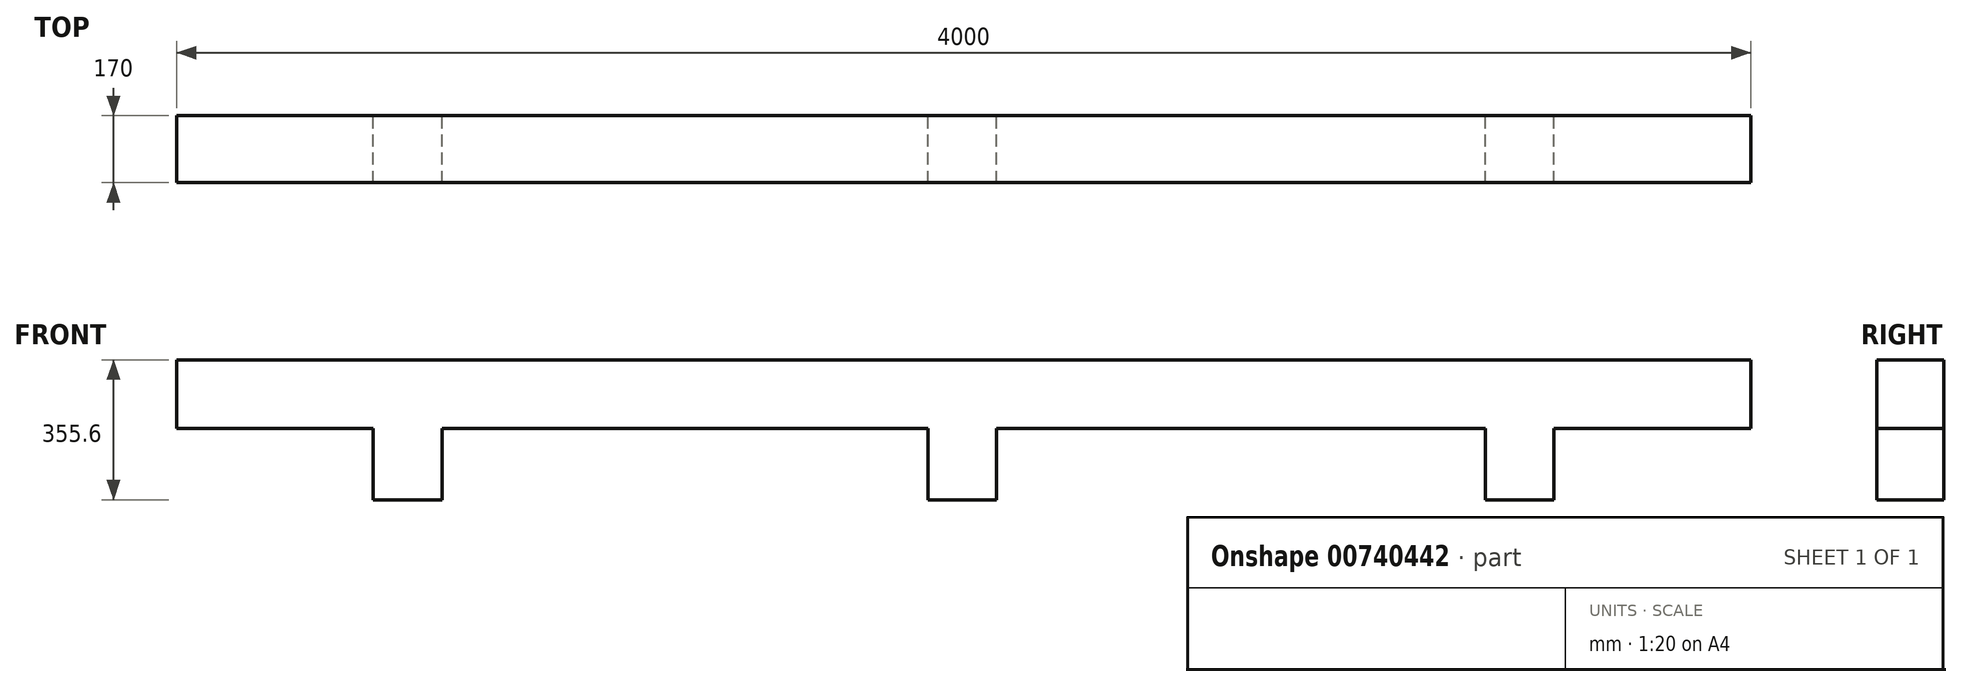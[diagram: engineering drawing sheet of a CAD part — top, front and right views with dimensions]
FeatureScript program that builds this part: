
annotation { "Feature Type Name" : "Feature", "Feature Type Description" : "" }
export const myFeature = defineFeature(function(context is Context, id is Id, definition is map)
    precondition{}
    {
        {
            var Q0;
            Q0=qCreatedBy(makeId("Front.planeOp"),FACE);
            var sketch = newSketch(context, id + "F0", { "sketchPlane" : qUnion([Q0])});
            skLineSegment(sketch, "E0", {"start": v(2000, 0) * mm, "end": v(-2000, 0) * mm, "construction": true});
            skLineSegment(sketch, "E1.bottom", {"start": v(-1997.52, 180.6) * mm, "end": v(-1497.52, 180.6) * mm});
            skLineSegment(sketch, "E1.top", {"start": v(-1997.52, 355.6) * mm, "end": v(2002.48, 355.6) * mm});
            skLineSegment(sketch, "E1.left", {"start": v(-1997.52, 180.6) * mm, "end": v(-1997.52, 355.6) * mm});
            skLineSegment(sketch, "E1.right", {"start": v(2002.48, 180.6) * mm, "end": v(2002.48, 355.6) * mm});
            skLineSegment(sketch, "E2.top", {"start": v(-1497.52, 0) * mm, "end": v(-1322.52, 0) * mm});
            skLineSegment(sketch, "E2.left", {"start": v(-1497.52, 180.6) * mm, "end": v(-1497.52, 0) * mm});
            skLineSegment(sketch, "E2.right", {"start": v(-1322.52, 180.6) * mm, "end": v(-1322.52, 0) * mm});
            skLineSegment(sketch, "E3.top", {"start": v(1502.48, 0) * mm, "end": v(1327.48, 0) * mm});
            skLineSegment(sketch, "E3.left", {"start": v(1502.48, 180.6) * mm, "end": v(1502.48, 0) * mm});
            skLineSegment(sketch, "E3.right", {"start": v(1327.48, 180.6) * mm, "end": v(1327.48, 0) * mm});
            skLineSegment(sketch, "E4.bottom", {"start": v(86.36, 0) * mm, "end": v(-88.64, 0) * mm});
            skLineSegment(sketch, "E4.left", {"start": v(86.36, 0) * mm, "end": v(86.36, 180.6) * mm});
            skLineSegment(sketch, "E4.right", {"start": v(-88.64, 0) * mm, "end": v(-88.64, 180.6) * mm});
            skLineSegment(sketch, "E5.trimOffspring", {"start": v(86.36, 180.6) * mm, "end": v(1327.48, 180.6) * mm});
            skLineSegment(sketch, "E6.trimOffspring", {"start": v(-1322.52, 180.6) * mm, "end": v(-88.64, 180.6) * mm});
            skLineSegment(sketch, "E7.trimOffspring", {"start": v(1502.48, 180.6) * mm, "end": v(2002.48, 180.6) * mm});
            skSolve(sketch);
        }
        {
            var Q0;
            Q0=makeQuery(id+"F0.imprint","IMPRINT",FACE,{"disambiguationData":[TD([[makeQuery(id+"F0.imprint","IMPRINT",EDGE,{"derivedFrom":sQuery(id+"F0.wireOp",EDGE,"E1.bottom")}),1.0]])]});
            extrude(context, id + "F1", {"entities" : qUnion([Q0]), "depth" : 170 * mm, "offsetDistance" : 25 * mm, "symmetric" : true});
        }
    });
